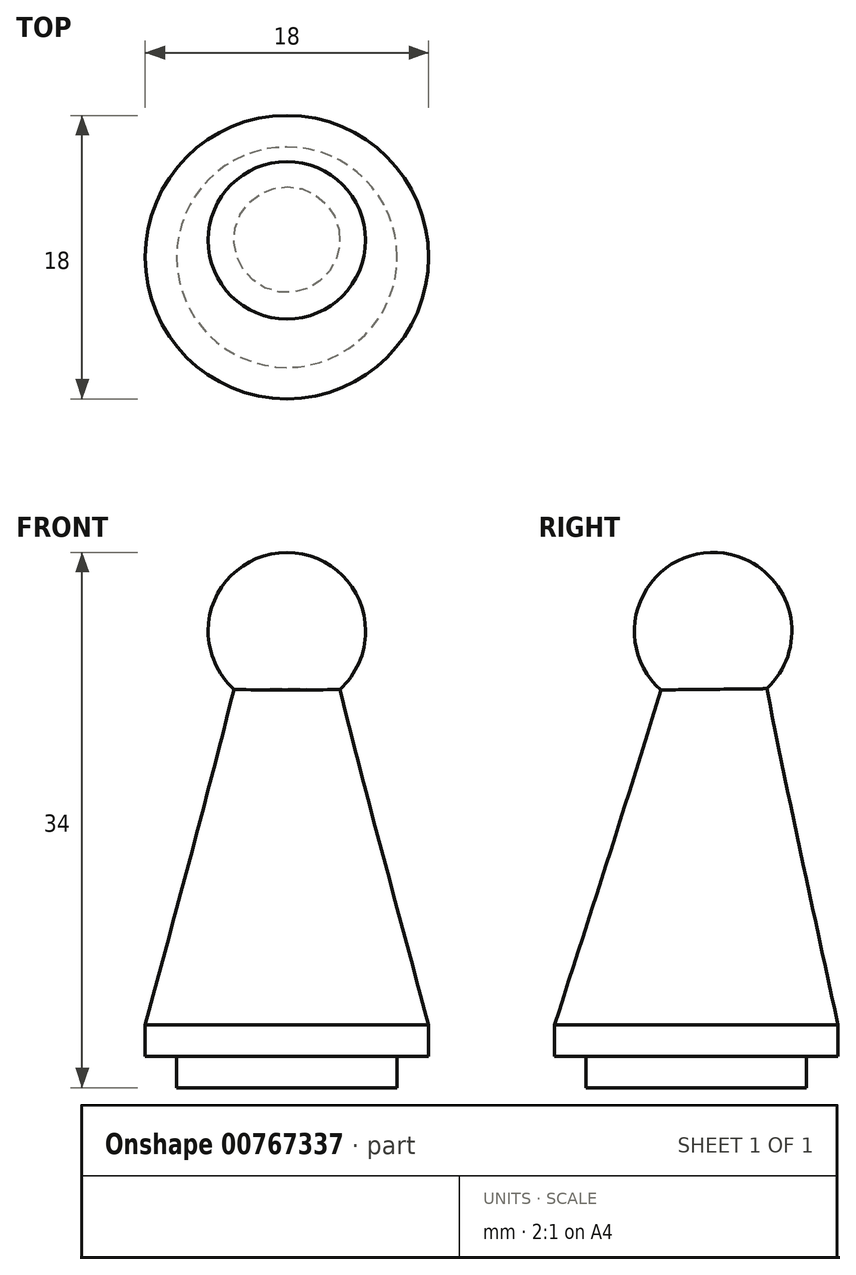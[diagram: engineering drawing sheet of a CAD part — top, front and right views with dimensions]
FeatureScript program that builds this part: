
annotation { "Feature Type Name" : "Feature", "Feature Type Description" : "" }
export const myFeature = defineFeature(function(context is Context, id is Id, definition is map)
    precondition{}
    {
        {
            var Q0;
            Q0=qCreatedBy(makeId("Top.planeOp"),FACE);
            var sketch = newSketch(context, id + "F0", { "sketchPlane" : qUnion([Q0])});
            skCircle(sketch, "E0", {"center": v(0, 0) * mm, "radius": 7 * mm});
            skSolve(sketch);
        }
        {
            var Q0;
            Q0=makeQuery(id+"F0.imprint","IMPRINT",FACE,{"disambiguationData":[TD([[makeQuery(id+"F0.imprint","IMPRINT",EDGE,{"derivedFrom":sQuery(id+"F0.wireOp",EDGE,"E0")}),1.0]])]});
            extrude(context, id + "F1", {"entities" : qUnion([Q0]), "depth" : 2 * mm, "offsetDistance" : 25 * mm});
        }
        {
            var Q0;
            Q0=makeQuery(id+"F1.opExtrude","CAP_FACE",FACE,{"disambiguationData":[OSD([sQuery(id+"F0.wireOp",EDGE,"E0")])],"isStart":false});
            var sketch = newSketch(context, id + "F2", { "sketchPlane" : qUnion([Q0])});
            skCircle(sketch, "E1", {"center": v(0, 0) * mm, "radius": 9 * mm});
            skSolve(sketch);
        }
        {
            var Q0;
            Q0=makeQuery(id+"F2.imprint","IMPRINT",FACE,{"disambiguationData":[TD([[makeQuery(id+"F2.imprint","IMPRINT",EDGE,{"derivedFrom":sQuery(id+"F2.wireOp",EDGE,"E1")}),1.0]])]});
            var Q1;
            Q1=makeQuery(id+"F2.imprint","IMPRINT",FACE,{"disambiguationData":[TD([[makeQuery(id+"F2.imprint","IMPRINT",EDGE,{"derivedFrom":makeQuery(id+"F1.opExtrude","CAP_EDGE",EDGE,{"disambiguationData":[OSD([sQuery(id+"F0.wireOp",EDGE,"E0")])],"isStart":false})}),1.0]])]});
            extrude(context, id + "F3", {"entities" : qUnion([Q0, Q1]), "operationType" : NewBodyOperationType.ADD, "depth" : 2 * mm, "offsetDistance" : 25 * mm});
        }
        {
            var Q0;
            Q0=makeQuery(id+"F3.opExtrude","CAP_FACE",FACE,{"disambiguationData":[OSD([sQuery(id+"F2.wireOp",EDGE,"E1")])],"isStart":false});
            cPlane(context, id + "F4", {"entities" : qUnion([Q0]), "cplaneType" : CPlaneType.OFFSET, "offset" : 25 * mm, "width" : 150 * mm, "height" : 150 * mm});
        }
        {
            var Q0;
            Q0=qCreatedBy(id+"F4.planeOp",FACE);
            var sketch = newSketch(context, id + "F5", { "sketchPlane" : qUnion([Q0])});
            skCircle(sketch, "E2", {"center": v(0, 1.32) * mm, "radius": 2.5 * mm});
            skSolve(sketch);
        }
        {
            var Q0;
            Q0=makeQuery(id+"F5.imprint","IMPRINT",FACE,{"disambiguationData":[TD([[makeQuery(id+"F5.imprint","IMPRINT",EDGE,{"derivedFrom":sQuery(id+"F5.wireOp",EDGE,"E2")}),1.0]])]});
            var Q1;
            Q1=makeQuery(id+"F3.opExtrude","CAP_FACE",FACE,{"disambiguationData":[OSD([sQuery(id+"F2.wireOp",EDGE,"E1")])],"isStart":false});
            loft(context, id + "F6", {"sheetProfilesArray" : [{ "sheetProfileEntities" : qUnion([Q0]) }, { "sheetProfileEntities" : qUnion([Q1]) }]});
        }
        {
            var Q0;
            Q0=makeQuery(id+"F6.opLoft","CAP_FACE",FACE,{"disambiguationData":[OSD([makeQuery(id+"F5.imprint","IMPRINT",FACE,{"disambiguationData":[TD([[makeQuery(id+"F5.imprint","IMPRINT",EDGE,{"derivedFrom":sQuery(id+"F5.wireOp",EDGE,"E2")}),1.0]])]})])],"isStart":true});
            var sketch = newSketch(context, id + "F7", { "sketchPlane" : qUnion([Q0])});
            skCircle(sketch, "E3", {"center": v(0, 1.07) * mm, "radius": 5 * mm});
            skLineSegment(sketch, "E4", {"start": v(-5, 1.07) * mm, "end": v(5, 1.07) * mm});
            skSolve(sketch);
        }
        {
            var Q0;
            {var subQ0=sQuery(id+"F7.wireOp",EDGE,"E4");var subQ1=sQuery(id+"F7.wireOp",EDGE,"E3");var subQ2=makeQuery(id+"F7.imprint","INTERSECT",VERTEX,{"disambiguationData":[OD(0.0)],"derivedFrom":[subQ1,subQ0]});Q0=makeQuery(id+"F7.imprint","IMPRINT",FACE,{"disambiguationData":[TD([[makeQuery(id+"F7.imprint","IMPRINT",EDGE,{"disambiguationData":[TD([[subQ2,1.0]])],"derivedFrom":subQ1}),1.0]])]});}
            var Q1;
            {var subQ0=sQuery(id+"F7.wireOp",EDGE,"E4");var subQ1=makeQuery(id+"F6.opLoft","MID_CAP_EDGE",EDGE,{"disambiguationData":[OSD([sQuery(id+"F5.wireOp",EDGE,"E2")])],"capPos":0.0});var subQ2=makeQuery(id+"F7.imprint","INTERSECT",VERTEX,{"disambiguationData":[OD(0.0)],"derivedFrom":[subQ1,subQ0]});Q1=makeQuery(id+"F7.imprint","IMPRINT",FACE,{"disambiguationData":[TD([[makeQuery(id+"F7.imprint","IMPRINT",EDGE,{"disambiguationData":[TD([[subQ2,-1.0]])],"derivedFrom":subQ0}),1.0]])]});}
            var Q2;
            Q2=sQuery(id+"F7.wireOp",EDGE,"E4");
            revolve(context, id + "F8", {"operationType" : NewBodyOperationType.ADD, "surfaceOperationType" : NewSurfaceOperationType.NEW, "entities" : qUnion([Q0, Q1]), "axis" : qUnion([Q2]), "revolveType" : RevolveType.FULL});
        }
    });
